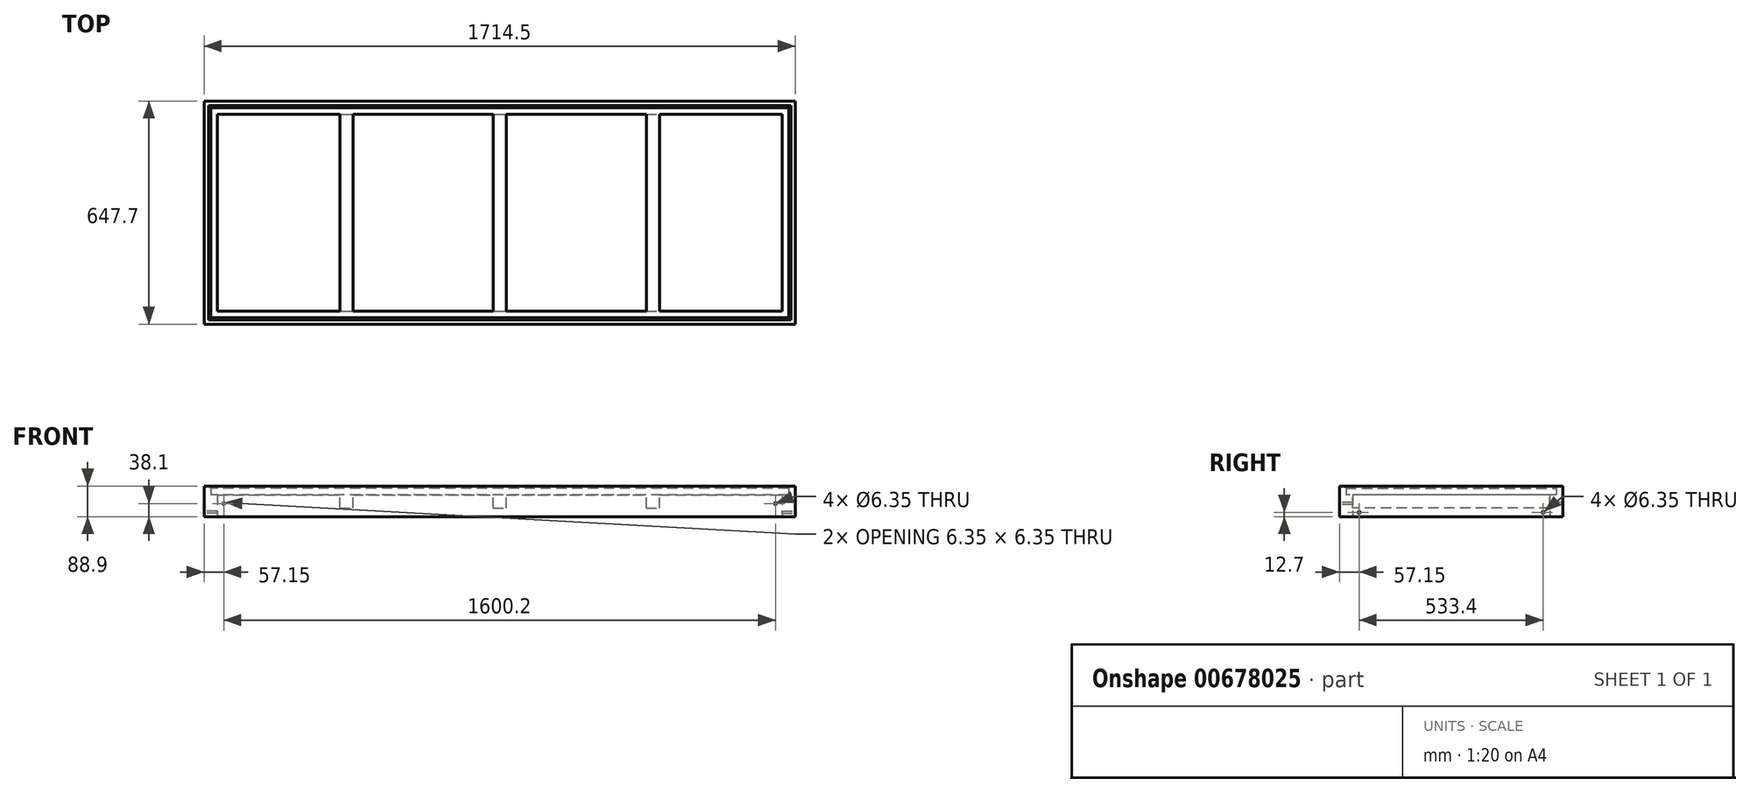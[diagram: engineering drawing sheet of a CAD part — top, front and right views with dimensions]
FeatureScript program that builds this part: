
annotation { "Feature Type Name" : "Feature", "Feature Type Description" : "" }
export const myFeature = defineFeature(function(context is Context, id is Id, definition is map)
    precondition{}
    {
        {
            var Q0;
            Q0=qCreatedBy(makeId("Top.planeOp"),FACE);
            var sketch = newSketch(context, id + "F0", { "sketchPlane" : qUnion([Q0])});
            skLineSegment(sketch, "E0.bottom", {"start": v(857.25, 323.85) * mm, "end": v(-857.25, 323.85) * mm});
            skLineSegment(sketch, "E0.top", {"start": v(857.25, -323.85) * mm, "end": v(-857.25, -323.85) * mm});
            skLineSegment(sketch, "E0.left", {"start": v(857.25, 323.85) * mm, "end": v(857.25, -323.85) * mm});
            skLineSegment(sketch, "E0.right", {"start": v(-857.25, 323.85) * mm, "end": v(-857.25, -323.85) * mm});
            skPoint(sketch, "E0.middle", {"position": v(0, 0) * mm});
            skLineSegment(sketch, "E1.bottom", {"start": v(838.2, 304.8) * mm, "end": v(-838.2, 304.8) * mm});
            skLineSegment(sketch, "E1.top", {"start": v(838.2, -304.8) * mm, "end": v(-838.2, -304.8) * mm});
            skLineSegment(sketch, "E1.left", {"start": v(838.2, 304.8) * mm, "end": v(838.2, -304.8) * mm});
            skLineSegment(sketch, "E1.right", {"start": v(-838.2, 304.8) * mm, "end": v(-838.2, -304.8) * mm});
            skSolve(sketch);
        }
        {
            var Q0;
            Q0 = qSketchRegion(id + "F0", true);
            extrude(context, id + "F1", {"entities" : qUnion([Q0]), "depth" : 88.9 * mm, "offsetDistance" : 25.4 * mm});
        }
        {
            var Q0;
            Q0=makeQuery(id+"F1.opExtrude","CAP_FACE",FACE,{"disambiguationData":[OSD([sQuery(id+"F0.wireOp",EDGE,"E0.bottom"),sQuery(id+"F0.wireOp",EDGE,"E0.top"),sQuery(id+"F0.wireOp",EDGE,"E0.left"),sQuery(id+"F0.wireOp",EDGE,"E0.right"),sQuery(id+"F0.wireOp",EDGE,"E1.bottom"),sQuery(id+"F0.wireOp",EDGE,"E1.top"),sQuery(id+"F0.wireOp",EDGE,"E1.left"),sQuery(id+"F0.wireOp",EDGE,"E1.right")])],"isStart":true});
            var sketch = newSketch(context, id + "F2", { "sketchPlane" : qUnion([Q0])});
            skLineSegment(sketch, "E2.bottom", {"start": v(-838.2, -304.8) * mm, "end": v(838.2, -304.8) * mm});
            skLineSegment(sketch, "E2.top", {"start": v(-838.2, 304.8) * mm, "end": v(838.2, 304.8) * mm});
            skLineSegment(sketch, "E2.left", {"start": v(-838.2, -304.8) * mm, "end": v(-838.2, 304.8) * mm});
            skLineSegment(sketch, "E2.right", {"start": v(838.2, -304.8) * mm, "end": v(838.2, 304.8) * mm});
            skPoint(sketch, "E2.middle", {"position": v(0, 0) * mm});
            skLineSegment(sketch, "E3.bottom", {"start": v(-819.15, -285.75) * mm, "end": v(819.15, -285.75) * mm});
            skLineSegment(sketch, "E3.top", {"start": v(-819.15, 285.75) * mm, "end": v(819.15, 285.75) * mm});
            skLineSegment(sketch, "E3.left", {"start": v(-819.15, -285.75) * mm, "end": v(-819.15, 285.75) * mm});
            skLineSegment(sketch, "E3.right", {"start": v(819.15, -285.75) * mm, "end": v(819.15, 285.75) * mm});
            skSolve(sketch);
        }
        {
            var Q0;
            Q0 = qSketchRegion(id + "F2", true);
            extrude(context, id + "F3", {"entities" : qUnion([Q0]), "operationType" : NewBodyOperationType.ADD, "oppositeDirection" : true, "depth" : 63.5 * mm, "offsetDistance" : 25.4 * mm});
        }
        {
            var Q0;
            Q0=makeQuery(id+"F3.opExtrude","CAP_FACE",FACE,{"disambiguationData":[OSD([sQuery(id+"F2.wireOp",EDGE,"E2.bottom"),sQuery(id+"F2.wireOp",EDGE,"E2.top"),sQuery(id+"F2.wireOp",EDGE,"E2.left"),sQuery(id+"F2.wireOp",EDGE,"E2.right"),sQuery(id+"F2.wireOp",EDGE,"E3.bottom"),sQuery(id+"F2.wireOp",EDGE,"E3.top"),sQuery(id+"F2.wireOp",EDGE,"E3.left"),sQuery(id+"F2.wireOp",EDGE,"E3.right")])],"isStart":false});
            var sketch = newSketch(context, id + "F4", { "sketchPlane" : qUnion([Q0])});
            skLineSegment(sketch, "E4.bottom", {"start": v(-19.05, 285.75) * mm, "end": v(19.05, 285.75) * mm});
            skLineSegment(sketch, "E4.top", {"start": v(-19.05, -285.75) * mm, "end": v(19.05, -285.75) * mm});
            skLineSegment(sketch, "E4.left", {"start": v(-19.05, 285.75) * mm, "end": v(-19.05, -285.75) * mm});
            skLineSegment(sketch, "E4.right", {"start": v(19.05, 285.75) * mm, "end": v(19.05, -285.75) * mm});
            skLineSegment(sketch, "E5.bottom", {"start": v(425.45, 285.75) * mm, "end": v(463.55, 285.75) * mm});
            skLineSegment(sketch, "E5.top", {"start": v(425.45, -285.75) * mm, "end": v(463.55, -285.75) * mm});
            skLineSegment(sketch, "E5.left", {"start": v(425.45, 285.75) * mm, "end": v(425.45, -285.75) * mm});
            skLineSegment(sketch, "E5.right", {"start": v(463.55, 285.75) * mm, "end": v(463.55, -285.75) * mm});
            skLineSegment(sketch, "E6.bottom", {"start": v(-463.55, 285.75) * mm, "end": v(-425.45, 285.75) * mm});
            skLineSegment(sketch, "E6.top", {"start": v(-463.55, -285.75) * mm, "end": v(-425.45, -285.75) * mm});
            skLineSegment(sketch, "E6.left", {"start": v(-463.55, 285.75) * mm, "end": v(-463.55, -285.75) * mm});
            skLineSegment(sketch, "E6.right", {"start": v(-425.45, 285.75) * mm, "end": v(-425.45, -285.75) * mm});
            skSolve(sketch);
        }
        {
            var Q0;
            Q0 = qSketchRegion(id + "F4", true);
            extrude(context, id + "F5", {"entities" : qUnion([Q0]), "operationType" : NewBodyOperationType.ADD, "oppositeDirection" : true, "depth" : 38.1 * mm, "offsetDistance" : 25.4 * mm});
        }
        {
            var Q0;
            Q0=makeQuery(id+"F1.opExtrude","SWEPT_FACE",FACE,{"disambiguationData":[OSD([sQuery(id+"F0.wireOp",EDGE,"E0.top")])]});
            var sketch = newSketch(context, id + "F6", { "sketchPlane" : qUnion([Q0])});
            skCircle(sketch, "E7", {"center": v(-800.1, 38.1) * mm, "radius": 3.18 * mm});
            skCircle(sketch, "E8", {"center": v(800.1, 38.1) * mm, "radius": 3.18 * mm});
            skSolve(sketch);
        }
        {
            var Q0;
            Q0 = qSketchRegion(id + "F6", true);
            extrude(context, id + "F7", {"entities" : qUnion([Q0]), "operationType" : NewBodyOperationType.REMOVE, "endBound" : BoundingType.THROUGH_ALL, "oppositeDirection" : true, "depth" : 25.4 * mm, "offsetDistance" : 25.4 * mm});
        }
        {
            var Q0;
            Q0=makeQuery(id+"F1.opExtrude","SWEPT_FACE",FACE,{"disambiguationData":[OSD([sQuery(id+"F0.wireOp",EDGE,"E0.right")])]});
            var sketch = newSketch(context, id + "F8", { "sketchPlane" : qUnion([Q0])});
            skCircle(sketch, "E9", {"center": v(-266.7, 12.7) * mm, "radius": 3.18 * mm});
            skCircle(sketch, "E10", {"center": v(266.7, 12.7) * mm, "radius": 3.18 * mm});
            skSolve(sketch);
        }
        {
            var Q0;
            Q0 = qSketchRegion(id + "F8", true);
            extrude(context, id + "F9", {"entities" : qUnion([Q0]), "operationType" : NewBodyOperationType.REMOVE, "oppositeDirection" : true, "depth" : 50.8 * mm, "offsetDistance" : 25.4 * mm});
        }
        {
            var Q0;
            Q0=makeQuery(id+"F1.opExtrude","SWEPT_FACE",FACE,{"disambiguationData":[OSD([sQuery(id+"F0.wireOp",EDGE,"E0.left")])]});
            var sketch = newSketch(context, id + "F10", { "sketchPlane" : qUnion([Q0])});
            skCircle(sketch, "E11", {"center": v(-266.7, 12.7) * mm, "radius": 3.18 * mm});
            skCircle(sketch, "E12", {"center": v(266.7, 12.7) * mm, "radius": 3.18 * mm});
            skSolve(sketch);
        }
        {
            var Q0;
            Q0 = qSketchRegion(id + "F10", true);
            extrude(context, id + "F11", {"entities" : qUnion([Q0]), "operationType" : NewBodyOperationType.REMOVE, "oppositeDirection" : true, "depth" : 50.8 * mm, "offsetDistance" : 25.4 * mm});
        }
        {
            var Q0;
            Q0=makeQuery(id+"F1.opExtrude","CAP_EDGE",EDGE,{"disambiguationData":[OSD([sQuery(id+"F0.wireOp",EDGE,"E1.bottom")])],"isStart":false});
            var Q1;
            Q1=makeQuery(id+"F1.opExtrude","CAP_EDGE",EDGE,{"disambiguationData":[OSD([sQuery(id+"F0.wireOp",EDGE,"E1.left")])],"isStart":false});
            var Q2;
            Q2=makeQuery(id+"F1.opExtrude","CAP_EDGE",EDGE,{"disambiguationData":[OSD([sQuery(id+"F0.wireOp",EDGE,"E1.right")])],"isStart":false});
            var Q3;
            Q3=makeQuery(id+"F1.opExtrude","CAP_EDGE",EDGE,{"disambiguationData":[OSD([sQuery(id+"F0.wireOp",EDGE,"E1.top")])],"isStart":false});
            chamfer(context, id + "F12", {"entities" : qUnion([Q0, Q1, Q2, Q3]), "width" : 6.35 * mm, "tangentPropagation" : true});
        }
    });
